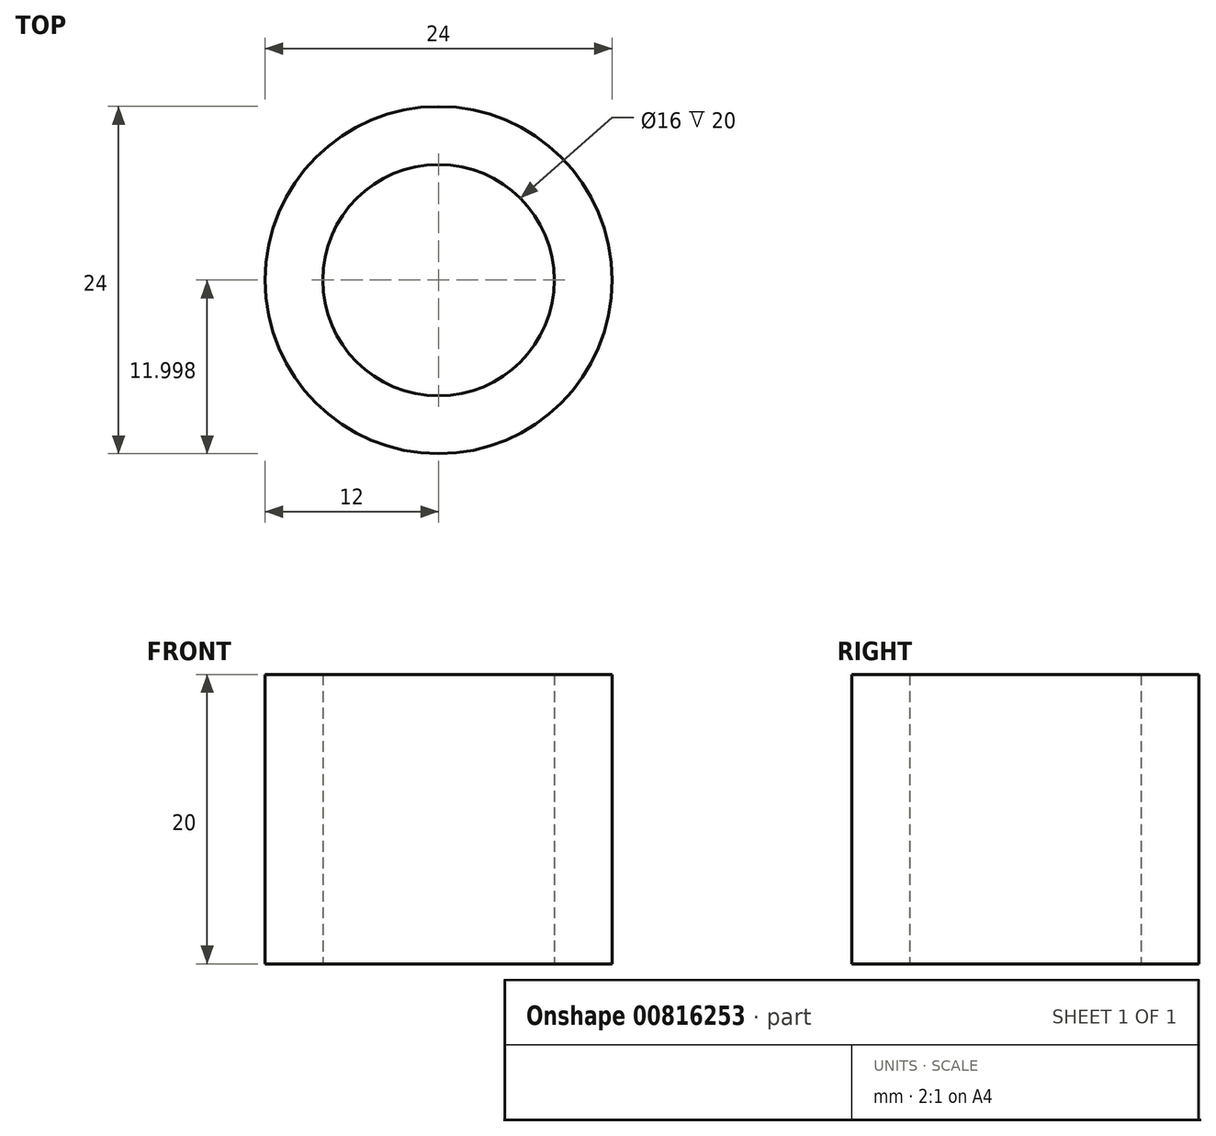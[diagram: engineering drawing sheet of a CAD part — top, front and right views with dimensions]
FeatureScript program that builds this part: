
annotation { "Feature Type Name" : "Feature", "Feature Type Description" : "" }
export const myFeature = defineFeature(function(context is Context, id is Id, definition is map)
    precondition{}
    {
        {
            var Q0;
            Q0=qCreatedBy(makeId("Top.planeOp"),FACE);
            var sketch = newSketch(context, id + "F0", { "sketchPlane" : qUnion([Q0])});
            skCircle(sketch, "E0", {"center": v(1.16, 7.03) * mm, "radius": 8 * mm});
            skCircle(sketch, "E1", {"center": v(1.16, 7.03) * mm, "radius": 12 * mm});
            skSolve(sketch);
        }
        {
            var Q0;
            Q0 = qSketchRegion(id + "F0", true);
            var sketch = newSketch(context, id + "F1", { "sketchPlane" : qUnion([Q0])});
            skSolve(sketch);
        }
        {
            var Q0;
            Q0=makeQuery(id+"F1.imprint","IMPRINT",FACE,{"disambiguationData":[TD([[makeQuery(id+"F1.imprint","IMPRINT",EDGE,{"derivedFrom":makeQuery(id+"F0.imprint","IMPRINT",EDGE,{"derivedFrom":sQuery(id+"F0.wireOp",EDGE,"E0")})}),-1.0]])]});
            extrude(context, id + "F2", {"entities" : qUnion([Q0]), "depth" : 20 * mm, "offsetDistance" : 25 * mm});
        }
    });
